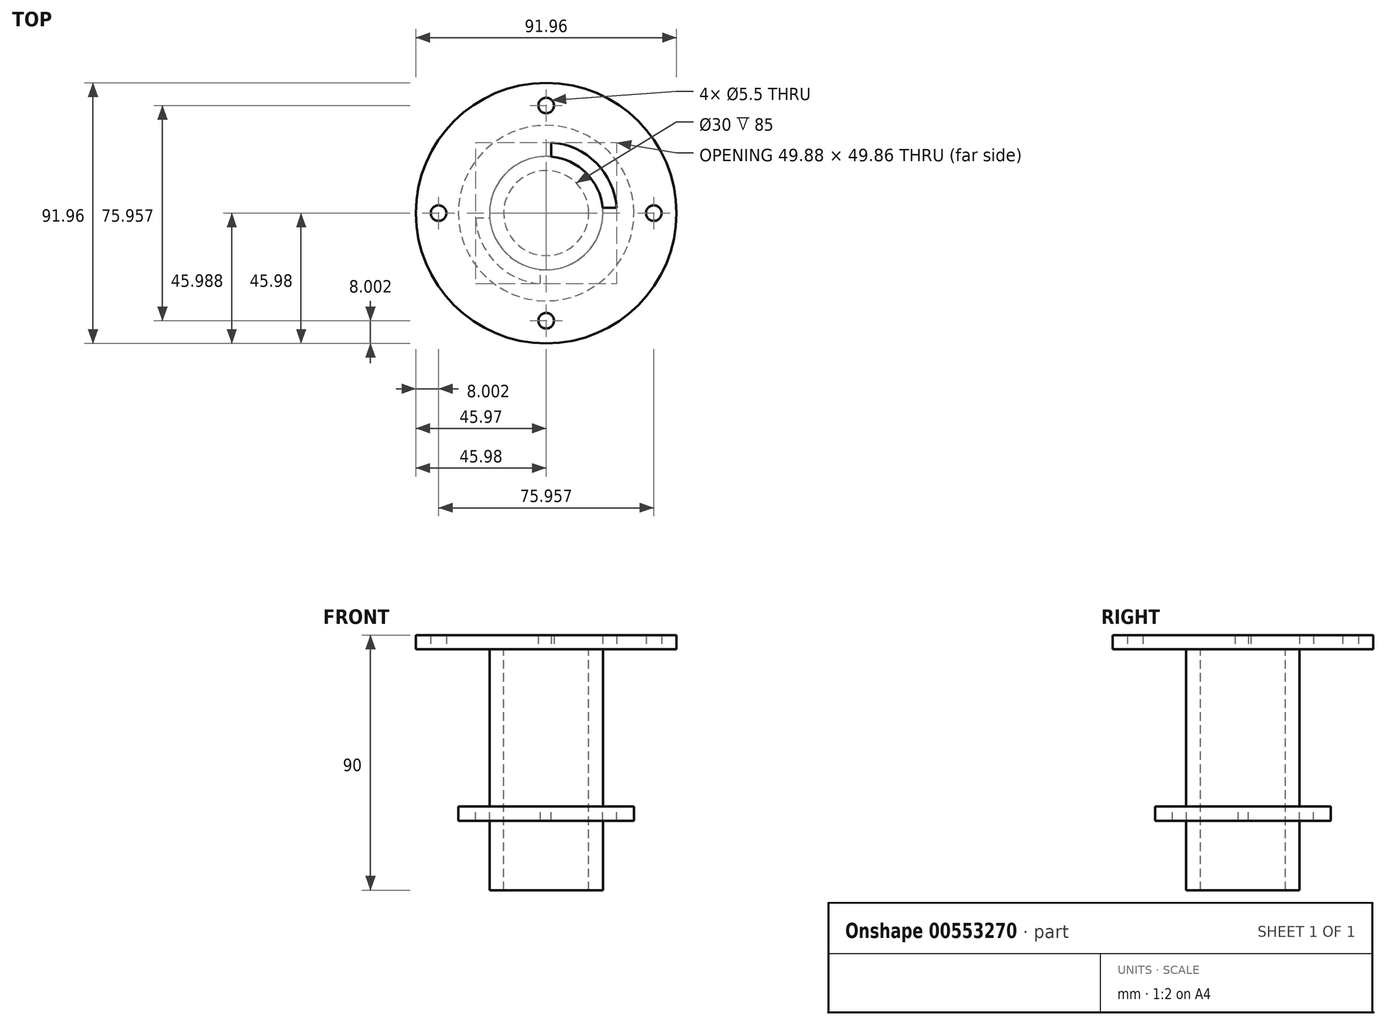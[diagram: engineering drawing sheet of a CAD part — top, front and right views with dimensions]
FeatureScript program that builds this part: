
annotation { "Feature Type Name" : "Feature", "Feature Type Description" : "" }
export const myFeature = defineFeature(function(context is Context, id is Id, definition is map)
    precondition{}
    {
        {
            var Q0;
            Q0=qCreatedBy(makeId("Top.planeOp"),FACE);
            var sketch = newSketch(context, id + "F0", { "sketchPlane" : qUnion([Q0])});
            skCircle(sketch, "E0", {"center": v(0, 0) * mm, "radius": 15 * mm});
            skCircle(sketch, "E1", {"center": v(0, 0) * mm, "radius": 20 * mm});
            skArc(sketch, "E2", {"start": v(-2, -24.92) * mm, "mid": v(-17.82, -17.54) * mm, "end": v(-24.95, -1.61) * mm});
            skArc(sketch, "E3", {"start": v(1.78, 24.94) * mm, "mid": v(17.64, 17.72) * mm, "end": v(24.93, 1.9) * mm});
            skLineSegment(sketch, "E4", {"start": v(24.93, 1.9) * mm, "end": v(19.9, 1.9) * mm});
            skLineSegment(sketch, "E5", {"start": v(1.78, 24.94) * mm, "end": v(1.78, 19.92) * mm});
            skLineSegment(sketch, "E6", {"start": v(-2, -24.92) * mm, "end": v(-2, -19.9) * mm});
            skLineSegment(sketch, "E7", {"start": v(-24.95, -1.61) * mm, "end": v(-19.93, -1.61) * mm});
            skCircle(sketch, "E8", {"center": v(0, 0) * mm, "radius": 30.98 * mm});
            skCircle(sketch, "E9", {"center": v(0, 0) * mm, "radius": 45.98 * mm});
            skPoint(sketch, "E10", {"position": v(0, 37.98) * mm});
            skPoint(sketch, "E11", {"position": v(37.98, 0) * mm});
            skPoint(sketch, "E12", {"position": v(0, -37.98) * mm});
            skPoint(sketch, "E13", {"position": v(-37.98, 0) * mm});
            skSolve(sketch);
        }
        {
            var Q0;
            Q0=makeQuery(id+"F0.imprint","IMPRINT",FACE,{"disambiguationData":[TD([[makeQuery(id+"F0.imprint","IMPRINT",EDGE,{"derivedFrom":sQuery(id+"F0.wireOp",EDGE,"E0")}),-1.0]])]});
            extrude(context, id + "F1", {"entities" : qUnion([Q0]), "oppositeDirection" : true, "depth" : 85 * mm, "offsetDistance" : 25 * mm});
        }
        {
            var Q0;
            Q0=makeQuery(id+"F0.imprint","IMPRINT",FACE,{"disambiguationData":[TD([[makeQuery(id+"F0.imprint","IMPRINT",EDGE,{"derivedFrom":sQuery(id+"F0.wireOp",EDGE,"E3")}),-1.0]])]});
            var Q1;
            Q1=makeQuery(id+"F0.imprint","IMPRINT",FACE,{"disambiguationData":[TD([[makeQuery(id+"F0.imprint","IMPRINT",EDGE,{"derivedFrom":sQuery(id+"F0.wireOp",EDGE,"E2")}),-1.0]])]});
            extrude(context, id + "F2", {"entities" : qUnion([Q0, Q1]), "operationType" : NewBodyOperationType.ADD, "oppositeDirection" : true, "depth" : 60.5 * mm, "offsetDistance" : 25 * mm, "hasSecondDirection" : true, "secondDirectionOppositeDirection" : true, "secondDirectionDepth" : 55.5 * mm});
        }
        {
            var Q0;
            Q0=makeQuery(id+"F0.imprint","IMPRINT",FACE,{"disambiguationData":[TD([[makeQuery(id+"F0.imprint","IMPRINT",EDGE,{"derivedFrom":sQuery(id+"F0.wireOp",EDGE,"E8")}),-1.0]])]});
            var Q1;
            Q1=makeQuery(id+"F0.imprint","IMPRINT",FACE,{"disambiguationData":[TD([[makeQuery(id+"F0.imprint","IMPRINT",EDGE,{"derivedFrom":sQuery(id+"F0.wireOp",EDGE,"E0")}),1.0]])]});
            var Q2;
            Q2=makeQuery(id+"F0.imprint","IMPRINT",FACE,{"disambiguationData":[TD([[makeQuery(id+"F0.imprint","IMPRINT",EDGE,{"derivedFrom":sQuery(id+"F0.wireOp",EDGE,"E0")}),-1.0]])]});
            var Q3;
            Q3=makeQuery(id+"F0.imprint","IMPRINT",FACE,{"disambiguationData":[TD([[makeQuery(id+"F0.imprint","IMPRINT",EDGE,{"derivedFrom":sQuery(id+"F0.wireOp",EDGE,"E3")}),-1.0]])]});
            var Q4;
            Q4=makeQuery(id+"F0.imprint","IMPRINT",FACE,{"disambiguationData":[TD([[makeQuery(id+"F0.imprint","IMPRINT",EDGE,{"derivedFrom":sQuery(id+"F0.wireOp",EDGE,"E2")}),1.0]])]});
            var Q5;
            Q5=makeQuery(id+"F0.imprint","IMPRINT",FACE,{"disambiguationData":[TD([[makeQuery(id+"F0.imprint","IMPRINT",EDGE,{"derivedFrom":sQuery(id+"F0.wireOp",EDGE,"E2")}),-1.0]])]});
            extrude(context, id + "F3", {"entities" : qUnion([Q0, Q1, Q2, Q3, Q4, Q5]), "operationType" : NewBodyOperationType.ADD, "depth" : 5 * mm, "offsetDistance" : 25 * mm});
        }
        {
            var Q0;
            Q0=sQuery(id+"F0.wireOp",VERTEX,"E10");
            var Q1;
            Q1=sQuery(id+"F0.wireOp",VERTEX,"E13");
            var Q2;
            Q2=sQuery(id+"F0.wireOp",VERTEX,"E12");
            var Q3;
            Q3=sQuery(id+"F0.wireOp",VERTEX,"E11");
            var Q4;
            Q4=makeQuery(id+"F1.opExtrude","SWEPT_BODY",BODY,{"disambiguationData":[OSD([sQuery(id+"F0.wireOp",EDGE,"E0"),sQuery(id+"F0.wireOp",EDGE,"E1")])]});
            hole(context, id + "F4", {"style" : HoleStyle.SIMPLE, "endStyle" : HoleEndStyle.THROUGH, "oppositeDirection" : true, "holeDiameter" : 5.5 * mm, "isTappedThrough" : true, "tappedDepth" : 12 * mm, "tapClearance" : 3, "locations" : qUnion([Q0, Q1, Q2, Q3]), "scope" : qUnion([Q4])});
        }
    });
